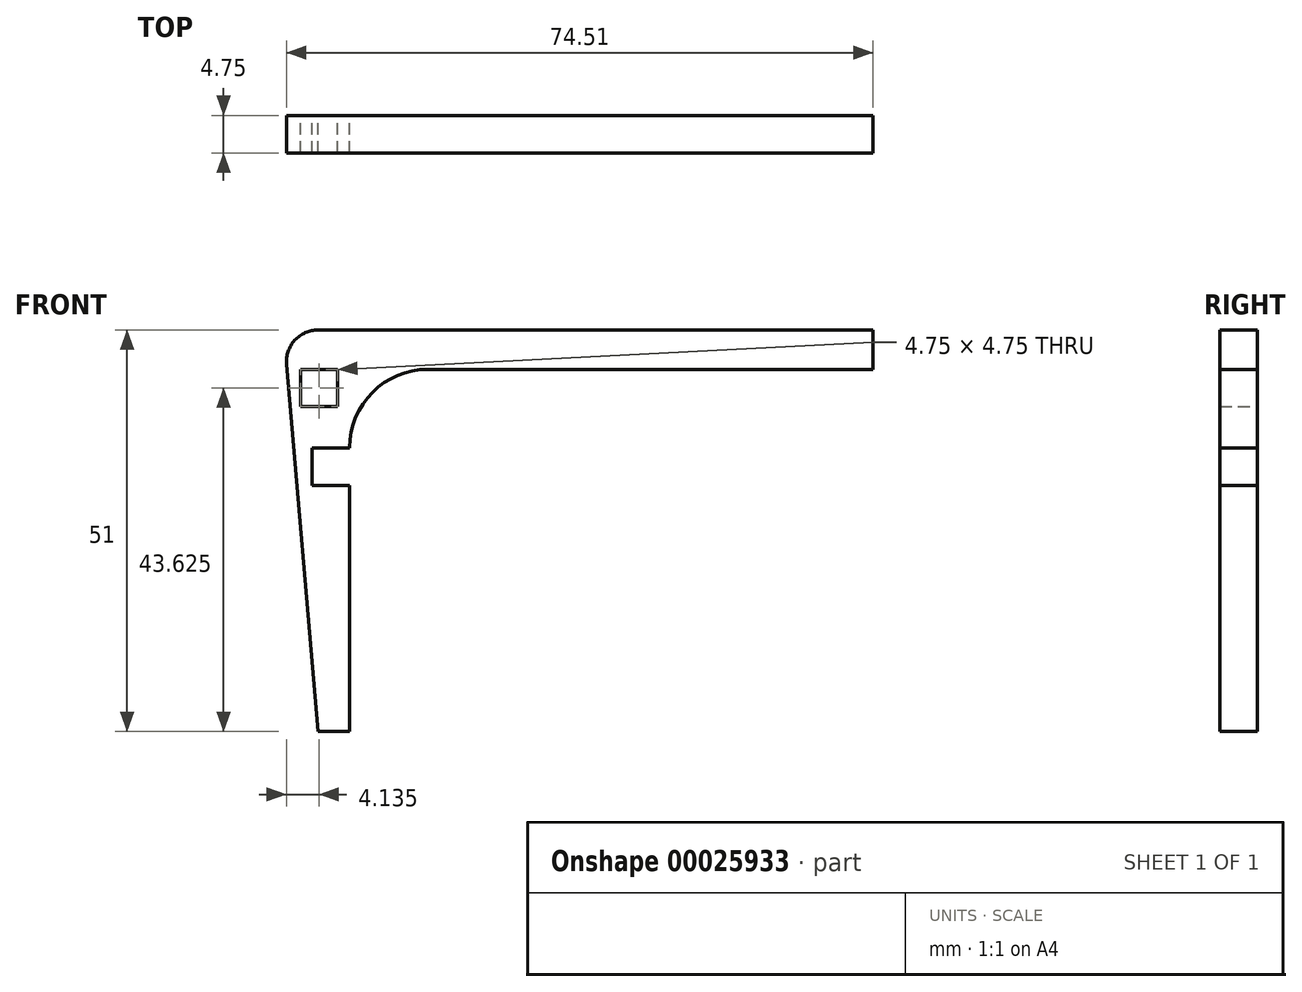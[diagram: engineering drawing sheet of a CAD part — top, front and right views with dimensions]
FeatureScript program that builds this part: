
annotation { "Feature Type Name" : "Feature", "Feature Type Description" : "" }
export const myFeature = defineFeature(function(context is Context, id is Id, definition is map)
    precondition{}
    {
        {
            var Q0;
            Q0=qCreatedBy(makeId("Front.planeOp"),FACE);
            var sketch = newSketch(context, id + "F0", { "sketchPlane" : qUnion([Q0])});
            skLineSegment(sketch, "E0", {"start": v(0, -46) * mm, "end": v(0, -9.95) * mm});
            skLineSegment(sketch, "E1", {"start": v(9.95, 0) * mm, "end": v(66.5, 0) * mm});
            skLineSegment(sketch, "E2", {"start": v(66.5, 0) * mm, "end": v(66.5, 5) * mm});
            skLineSegment(sketch, "E3", {"start": v(0, -46) * mm, "end": v(-4, -46) * mm});
            skLineSegment(sketch, "E4", {"start": v(66.5, 5) * mm, "end": v(-4, 5) * mm});
            skLineSegment(sketch, "E5", {"start": v(-4, -46) * mm, "end": v(-8, 0.64) * mm});
            skArc(sketch, "E6", {"start": v(-8, 0.64) * mm, "mid": v(-6.96, 3.7) * mm, "end": v(-4, 5) * mm});
            skLineSegment(sketch, "E7.bottom", {"start": v(-1.5, 0) * mm, "end": v(-6.25, 0) * mm});
            skLineSegment(sketch, "E7.top", {"start": v(-1.5, -4.75) * mm, "end": v(-6.25, -4.75) * mm});
            skLineSegment(sketch, "E7.left", {"start": v(-1.5, 0) * mm, "end": v(-1.5, -4.75) * mm});
            skLineSegment(sketch, "E7.right", {"start": v(-6.25, 0) * mm, "end": v(-6.25, -4.75) * mm});
            skLineSegment(sketch, "E8", {"start": v(0, -10) * mm, "end": v(-4.75, -10) * mm});
            skLineSegment(sketch, "E9", {"start": v(-4.75, -10) * mm, "end": v(-4.75, -14.75) * mm});
            skLineSegment(sketch, "E10", {"start": v(-4.75, -14.75) * mm, "end": v(0, -14.75) * mm});
            skPoint(sketch, "E11.visualSharp", {"position": v(0, 0) * mm});
            skArc(sketch, "E11.filletArc", {"start": v(9.95, 0) * mm, "mid": v(2.91, -2.91) * mm, "end": v(0, -9.95) * mm});
            skSolve(sketch);
        }
        {
            var Q0;
            Q0=makeQuery(id+"F0.imprint","IMPRINT",FACE,{"disambiguationData":[TD([[makeQuery(id+"F0.imprint","IMPRINT",EDGE,{"derivedFrom":sQuery(id+"F0.wireOp",EDGE,"E0")}),1.0]])]});
            extrude(context, id + "F1", {"entities" : qUnion([Q0]), "depth" : 4.75 * mm});
        }
    });
